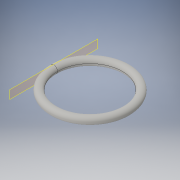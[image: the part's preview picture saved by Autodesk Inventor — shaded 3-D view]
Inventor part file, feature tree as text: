
AUTODESK INVENTOR PART (.ipt)
format: ipt  version: 2016 (Build 200138000, 138)  size: 143,872 bytes
history: native  units: in
note: dims shown in document units (in); Inventor stores cm internally (conversion verified against a paired STEP export)
features: sketch x2, sweep x1
ambient origin geometry x8: Origin, YZ Plane, XZ Plane, XY Plane, X Axis, Y Axis, Z Axis, Center Point
bodies: Solid1 (feature_tree)
feature tree (3):
  sweep  "Sweep1"
  sketch  "Sketch1"  dims[d0=0.197in d1=1.856in]
  sketch  "Sketch2"  dims[d2=0.0in d3=0.0in]
